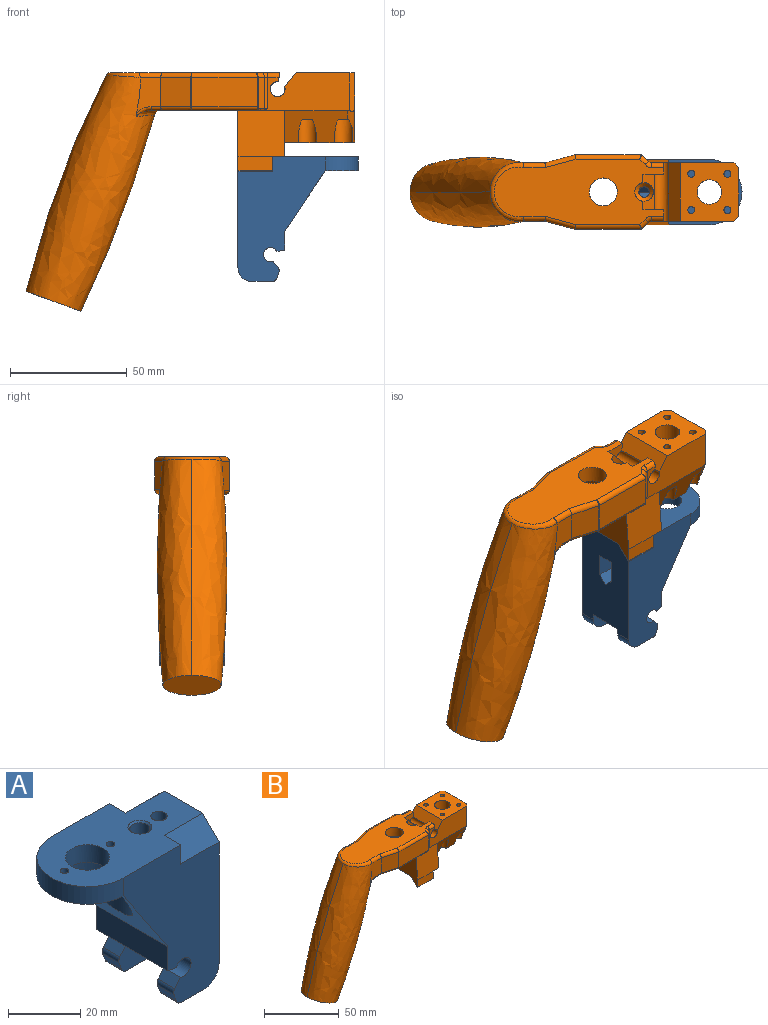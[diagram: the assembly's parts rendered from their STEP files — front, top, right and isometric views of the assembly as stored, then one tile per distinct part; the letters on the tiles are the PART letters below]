
ASSEMBLY  parts=2 mates=1
PART A: 52 faces, bbox 51.8x28x53.5 mm
  f0: cone r=1.4mm half-angle=59deg, axis (0,0,1), area 28.7mm2, adj f2
  f1: plane 13.5x0mm, normal (1,0,0), area 0mm2, adj f6,f7,f20,f22,f23
  f2: cylinder r=2.8mm len=7.5mm, axis (0,0,-1), area 131.9mm2, adj f0,f13
  f3: cylinder r=12.5mm len=25mm, axis (0,0,-1), area 464.3mm2, adj f4,f16
  f4: plane 28x26.99mm, normal (0,0,-1), area 426.9mm2, adj f3,f10,f11,f12,f15,f16
  f5: plane 6.11x6mm, normal (0,0,-1), area 28.3mm2, adj f17
  f6: plane 13.5x3.5mm, normal (0.87,-0.5,0), area 47.5mm2, adj f1,f20,f21,f22
  f7: plane 13.5x3.5mm, normal (0.87,0.5,0), area 47.5mm2, adj f1,f19,f20,f23
  f8: plane 6.5x6.5mm, normal (1,0,0), area 21.1mm2, adj f24,f25,f26
  f9: cylinder r=2.25mm len=12mm, axis (0,0,-1), area 169.6mm2, adj f20,f26
  f10: cylinder r=1.23mm len=6mm, axis (0,0,-1), area 46.4mm2, adj f4,f26
  f11: cylinder r=1.23mm len=6mm, axis (0,0,-1), area 46.4mm2, adj f4,f26
  f12: cylinder r=6.1mm len=12.2mm, axis (0,0,-1), area 230mm2, adj f4,f26
  f13: cone r=3.05mm half-angle=45deg, axis (0,0,1), area 13.6mm2, adj f2,f26
  f14: plane 6.5x6.5mm, normal (1,0,0), area 21.1mm2, adj f26,f27,f28
  f15: cylinder r=14mm len=28mm, axis (0,0,-1), area 263.9mm2, adj f4,f24,f26,f28
  f16: plane 28x26mm, normal (-0.83,0,-0.56), area 438mm2, adj f3,f4,f18,f24,f28
  f17: cylinder r=3mm len=6mm, axis (0,0,-1), area 94.2mm2, adj f5,f29
  f18: plane 28x8.14mm, normal (-1,0,0), area 227.9mm2, adj f16,f24,f28,f44
  f19: plane 11.52x10mm, normal (0,1,0), area 115.2mm2, adj f7,f20,f23,f45
  f20: plane 13.54x7mm, normal (0,0,-1), area 71.8mm2, adj f1,f6,f7,f9,f19,f21,f45
  f21: plane 11.52x10mm, normal (0,-1,0), area 115.2mm2, adj f6,f20,f22,f45
  f22: plane 13.54x3.5mm, normal (0,-0.71,0.71), area 62mm2, adj f1,f6,f21,f23,f45
  f23: plane 13.54x3.5mm, normal (0,0.71,0.71), area 62mm2, adj f1,f7,f19,f22,f45
  f24: plane 53.5x37.5mm, normal (0,1,0), area 1225.3mm2, adj f8,f15,f16,f18,f25,f26,f30,f31
  f25: plane 15x6.5mm, normal (0,0.71,0.71), area 137.9mm2, adj f8,f24,f26,f45
  f26: plane 51.76x28mm, normal (0,0,1), area 986.4mm2, adj f8,f9,f10,f11,f12,f13,f14,f15
  f27: plane 15x6.5mm, normal (0,-0.71,0.71), area 137.9mm2, adj f14,f26,f28,f45
  f28: plane 53.5x37.5mm, normal (0,-1,0), area 1225.3mm2, adj f14,f15,f16,f18,f26,f27,f37,f38
  f29: plane 8.15x8mm, normal (0,0,-1), area 22mm2, adj f17,f46
  f30: cylinder r=6mm len=6.5mm, axis (0,1,0), area 61.3mm2, adj f24,f31,f45,f47
  f31: plane 8.73x6.5mm, normal (0,0,-1), area 56.7mm2, adj f24,f30,f32,f47
  f32: cylinder r=2mm len=6.5mm, axis (0,1,0), area 15.8mm2, adj f24,f31,f33,f47
  f33: plane 6.5x2.66mm, normal (-0.94,0,-0.35), area 18.4mm2, adj f24,f32,f34,f47
  f34: cylinder r=2mm len=6.5mm, axis (0,-1,0), area 13.5mm2, adj f24,f33,f35,f47
  f35: plane 6.5x2.7mm, normal (-0.78,0,0.63), area 22.5mm2, adj f24,f34,f36,f47
  f36: cylinder r=3.05mm len=6.5mm, axis (0,-1,0), area 91.4mm2, adj f24,f35,f44,f47
  f37: cylinder r=6mm len=6.5mm, axis (0,1,0), area 61.3mm2, adj f28,f38,f45,f49
  f38: plane 8.73x6.5mm, normal (0,0,-1), area 56.7mm2, adj f28,f37,f39,f49
  f39: cylinder r=2mm len=6.5mm, axis (0,1,0), area 15.8mm2, adj f28,f38,f40,f49
  f40: plane 6.5x2.66mm, normal (-0.94,0,-0.35), area 18.4mm2, adj f28,f39,f41,f49
  f41: cylinder r=2mm len=6.5mm, axis (0,-1,0), area 13.5mm2, adj f28,f40,f42,f49
  f42: plane 6.5x2.7mm, normal (-0.78,0,0.63), area 22.5mm2, adj f28,f41,f43,f49
  f43: cylinder r=3.05mm len=6.5mm, axis (0,-1,0), area 91.4mm2, adj f28,f42,f44,f49
  f44: plane 28x3.28mm, normal (-0.16,0,-0.99), area 82.1mm2, adj f18,f24,f28,f36,f43,f47,f48,f49
  f45: plane 47.5x28mm, normal (1,0,0), area 1168mm2, adj f19,f20,f21,f22,f23,f24,f25,f26
  f46: cylinder r=4mm len=8mm, axis (0,0,1), area 175.9mm2, adj f29,f50
  f47: plane 17.74x15.25mm, normal (0,-1,0), area 145.3mm2, adj f30,f31,f32,f33,f34,f35,f36,f44
  f48: cylinder r=3.75mm len=15mm, axis (0,-1,0), area 153.6mm2, adj f44,f47,f49,f51
  f49: plane 17.74x15.25mm, normal (0,1,0), area 145.3mm2, adj f37,f38,f39,f40,f41,f42,f43,f44
  f50: plane 15x10.25mm, normal (0,0,-1), area 103.5mm2, adj f45,f46,f47,f49,f51
  f51: plane 15x2.96mm, normal (-1,0,0), area 44.4mm2, adj f47,f48,f49,f50
PART B: 105 faces, bbox 142.7x34x104.2 mm
  f0: plane 30.07x15.07mm, normal (0,0,-1), area 268.1mm2, adj f11,f12,f13,f28,f29,f45,f46,f97
  f1: cylinder r=1.5mm len=20mm, axis (0,0,1), area 188.5mm2, adj f43,f104
  f2: cylinder r=1.5mm len=20mm, axis (0,0,1), area 188.5mm2, adj f43,f101
  f3: cylinder r=1.5mm len=20mm, axis (0,0,1), area 188.5mm2, adj f43,f100
  f4: cylinder r=1.5mm len=20mm, axis (0,0,1), area 188.5mm2, adj f43,f98
  f5: plane 3.4x3.4mm, normal (0,0,-1), area 9.1mm2, adj f6
  f6: cone r=2.2mm half-angle=45deg, axis (0,0,1), area 19.5mm2, adj f5,f8
  f7: plane 6.5x6mm, normal (1,0,0), area 21mm2, adj f14,f15,f16,f17
  f8: cylinder r=2.7mm len=5.4mm, axis (0,0,-1), area 84.8mm2, adj f6,f17
  f9: plane 6.5x6mm, normal (1,0,0), area 21mm2, adj f17,f18,f19,f20
  f10: sphere r=1.5mm, area 0.6mm2, adj f24,f35,f36
  f11: cylinder r=5.25mm len=30mm, axis (0,0,-1), area 989.6mm2, adj f0,f43
  f12: plane 30x21mm, normal (1,0,0), area 524.6mm2, adj f0,f29,f30,f43,f44,f45
  f13: plane 28x19.74mm, normal (1,0,0), area 248.3mm2, adj f0,f17,f27,f28,f46,f47
  f14: plane 15x6mm, normal (0,1,0), area 90mm2, adj f7,f15,f47,f48
  f15: plane 15x0.5mm, normal (0,0,-1), area 7.5mm2, adj f7,f14,f16,f48
  f16: plane 15x6mm, normal (0,-0.71,-0.71), area 127.3mm2, adj f7,f15,f17,f48
  f17: plane 28x20mm, normal (0,0,-1), area 326.2mm2, adj f7,f8,f9,f13,f16,f18,f27,f31
  f18: plane 15x6mm, normal (0,0.71,-0.71), area 127.3mm2, adj f9,f17,f19,f48
  f19: plane 15x0.5mm, normal (0,0,-1), area 7.5mm2, adj f9,f18,f20,f48
  f20: plane 15x6mm, normal (0,-1,0), area 90mm2, adj f9,f19,f27,f48
  f21: bspline ~7.63x4.68mm, area 16.4mm2, adj f32,f33,f51,f52
  f22: plane 25.35x23.5mm, normal (-0.34,0,-0.94), area 490.9mm2, adj f52,f53
  f23: bspline ~7.09x4.19mm, area 11.6mm2, adj f33,f34,f53,f54
  f24: cylinder r=1.5mm len=12.5mm, axis (0,0,-1), area 4.9mm2, adj f10,f55,f56,f57
  f25: cylinder r=0.5mm len=12.5mm, axis (0,0,-1), area 4.9mm2, adj f26,f57,f58,f59
  f26: bspline ~1.53x1.5mm, area 1.3mm2, adj f25,f36,f37,f59
  f27: plane 20x19.74mm, normal (0,-1,0.08), area 395.9mm2, adj f13,f17,f20,f48,f61
  f28: plane 28.45x15.19mm, normal (0,-0.94,-0.34), area 264.8mm2, adj f0,f13,f29,f61,f97,f98,f99,f100
  f29: cylinder r=3mm len=18.04mm, axis (0,0.34,-0.94), area 48.4mm2, adj f0,f12,f28,f30,f61,f99,f100
  f30: plane 16.78x2mm, normal (0.71,-0.71,0), area 46mm2, adj f12,f29,f43,f61
  f31: cylinder r=2.25mm len=19.25mm, axis (0,0,-1), area 272.1mm2, adj f17,f62
  f32: cylinder r=2mm len=3.9mm, axis (-1,0,0), area 11.8mm2, adj f21,f49,f51,f64
  f33: bspline ~29.82x10.55mm, area 107.4mm2, adj f21,f23,f52,f53,f64
  f34: cylinder r=1.5mm len=4.25mm, axis (1,0,0), area 9.8mm2, adj f23,f35,f54,f64
  f35: cylinder r=1.5mm len=13.45mm, axis (-0.97,0.26,0), area 31.6mm2, adj f10,f34,f55,f64
  f36: cylinder r=1.5mm len=29.03mm, axis (-1,0,0), area 67.2mm2, adj f10,f26,f57,f64
  f37: cylinder r=0.5mm len=2.12mm, axis (-0.71,-0.71,0), area 2mm2, adj f26,f38,f59,f64
  f38: torus R=2.5mm, axis (0,0,-1), area 0.8mm2, adj f37,f60,f61,f64
  f39: plane 16x8.8mm, normal (0,1,0), area 140.8mm2, adj f40,f48,f50,f64
  f40: plane 25x8.8mm, normal (1,0,0), area 220mm2, adj f39,f41,f50,f64
  f41: plane 16x8.8mm, normal (0,-1,0), area 140.8mm2, adj f40,f48,f50,f64
  f42: plane 25x6.04mm, normal (-0.77,0,0.63), area 195.2mm2, adj f43,f61,f63,f65
  f43: plane 25x25mm, normal (0,0,1), area 506.1mm2, adj f1,f2,f3,f4,f11,f12,f30,f42
  f44: plane 16.78x2mm, normal (0.71,0.71,0), area 46mm2, adj f12,f43,f45,f65
  f45: cylinder r=3mm len=18.04mm, axis (0,0.34,0.94), area 48.4mm2, adj f0,f12,f44,f46,f65,f101,f102
  f46: plane 28.45x15.19mm, normal (0,0.94,-0.34), area 264.8mm2, adj f0,f13,f45,f65,f101,f102,f103,f104
  f47: plane 20x19.74mm, normal (0,1,0.08), area 395.9mm2, adj f13,f14,f17,f48,f65
  f48: plane 34.8x28mm, normal (-1,0,0), area 791.6mm2, adj f14,f15,f16,f17,f18,f19,f20,f27
  f49: cylinder r=2mm len=13.83mm, axis (-0.97,-0.26,0), area 42.5mm2, adj f32,f64,f67,f68
  f50: plane 25x16mm, normal (0,0,-1), area 286.9mm2, adj f39,f40,f41,f48,f69
  f51: plane 14.97x10.47mm, normal (0,1,0), area 114.9mm2, adj f21,f32,f52,f68,f70
  f52: bspline ~101.19x59.53mm, area 4291.9mm2, adj f21,f22,f33,f51,f53,f70,f71
  f53: bspline ~101.19x59.53mm, area 4291.7mm2, adj f22,f23,f33,f52,f54,f71,f72
  f54: plane 15.33x10.54mm, normal (0,-1,0), area 119.3mm2, adj f23,f34,f53,f55,f72
  f55: plane 12.87x12.5mm, normal (-0.26,-0.97,0), area 166.6mm2, adj f24,f35,f54,f73
  f56: sphere r=2mm, area 0.6mm2, adj f24,f73,f74
  f57: plane 28.03x12.5mm, normal (0,-1,0), area 350.4mm2, adj f24,f25,f36,f74
  f58: torus R=1.55mm, axis (0.92,0.38,0), area 0.6mm2, adj f25,f74,f75
  f59: plane 13.71x2.97mm, normal (0.71,-0.71,0), area 52.5mm2, adj f25,f26,f37,f60,f75
  f60: cylinder r=2mm len=13.5mm, axis (0,0,-1), area 21.2mm2, adj f38,f59,f61,f76
  f61: plane 48.21x16.48mm, normal (0,-1,0), area 507.9mm2, adj f27,f28,f29,f30,f38,f42,f43,f48
  f62: cone r=3.12mm half-angle=45deg, axis (0,0,1), area 48.6mm2, adj f31,f80
  f63: cylinder r=3.2mm len=25mm, axis (0,1,0), area 343.3mm2, adj f42,f61,f65,f78,f79,f81,f82,f83
  f64: plane 48.4x28.52mm, normal (0,0,-1), area 555mm2, adj f32,f33,f34,f35,f36,f37,f38,f39
  f65: plane 48.21x16.48mm, normal (0,1,0), area 507.9mm2, adj f42,f43,f44,f45,f46,f47,f48,f63
  f66: torus R=2.5mm, axis (0,0,-1), area 0.8mm2, adj f64,f65,f85,f86
  f67: cylinder r=2mm len=29.73mm, axis (-1,0,0), area 90.6mm2, adj f49,f64,f88,f89
  f68: plane 13.06x12mm, normal (-0.26,0.97,0), area 162.3mm2, adj f49,f51,f87,f89
  f69: cylinder r=6mm len=12mm, axis (0,0,-1), area 271.4mm2, adj f50,f90
  f70: cylinder r=2mm len=9.42mm, axis (1,0,0), area 28.7mm2, adj f51,f52,f71,f87,f90
  f71: bspline ~25.37x15.2mm, area 103.4mm2, adj f52,f53,f70,f72,f90
  f72: cylinder r=2mm len=9.42mm, axis (-1,0,0), area 28.7mm2, adj f53,f54,f71,f73,f90
  f73: cylinder r=2mm len=13.64mm, axis (-0.97,0.26,0), area 42.2mm2, adj f55,f56,f72,f90
  f74: cylinder r=2mm len=28.03mm, axis (-1,0,0), area 87mm2, adj f56,f57,f58,f90
  f75: cylinder r=2mm len=4.18mm, axis (-0.71,-0.71,0), area 11.3mm2, adj f58,f59,f76,f90
  f76: torus R=4mm, axis (0,0,1), area 6.7mm2, adj f60,f75,f77,f90
  f77: cylinder r=2mm len=5.17mm, axis (-1,0,0), area 15.7mm2, adj f61,f76,f78,f90
  f78: plane 5.04x3.96mm, normal (0.99,0,-0.16), area 18.1mm2, adj f61,f63,f77,f79,f90
  f79: plane 8.97x6.04mm, normal (0,1,0), area 30.9mm2, adj f63,f78,f81,f90
  f80: cylinder r=4mm len=15mm, axis (0,0,-1), area 339.7mm2, adj f62,f81,f90
  f81: plane 16.95x7.79mm, normal (0.77,0,0.63), area 72.7mm2, adj f63,f79,f80,f82,f90
  f82: plane 8.97x6.04mm, normal (0,-1,0), area 30.9mm2, adj f63,f81,f83,f90
  f83: plane 5.04x3.96mm, normal (0.99,0,-0.16), area 18.1mm2, adj f63,f65,f82,f84,f90
  f84: cylinder r=2mm len=5.17mm, axis (1,0,0), area 15.7mm2, adj f65,f83,f90,f91
  f85: cylinder r=0.5mm len=1.62mm, axis (-0.71,0.71,0), area 1.4mm2, adj f64,f66,f88,f92
  f86: cylinder r=2mm len=13.5mm, axis (0,0,1), area 21.2mm2, adj f65,f66,f91,f92
  f87: cylinder r=2mm len=13.83mm, axis (-0.97,-0.26,0), area 42.5mm2, adj f68,f70,f90,f93
  f88: bspline ~2.04x2mm, area 1.8mm2, adj f67,f85,f92,f94
  f89: plane 28.23x12mm, normal (0,1,0), area 338.8mm2, adj f67,f68,f93,f94
  f90: plane 72.77x28.01mm, normal (0,0,1), area 1463.4mm2, adj f69,f70,f71,f72,f73,f74,f75,f76
  f91: torus R=4mm, axis (0,0,1), area 6.7mm2, adj f84,f86,f90,f95
  f92: plane 13.81x3.08mm, normal (0.71,0.71,0), area 52.2mm2, adj f85,f86,f88,f94,f95
  f93: cylinder r=2mm len=28.23mm, axis (-1,0,0), area 87.3mm2, adj f87,f89,f90,f96
  f94: cylinder r=0.5mm len=12mm, axis (0,0,-1), area 4.7mm2, adj f88,f89,f92,f96
  f95: cylinder r=2mm len=4.18mm, axis (-0.71,0.71,0), area 11.3mm2, adj f90,f91,f92,f96
  f96: bspline ~2.03x2mm, area 0.5mm2, adj f93,f94,f95
  f97: cylinder r=4mm len=10mm, axis (0,0,-1), area 163.6mm2, adj f0,f28,f98
  f98: plane 8x7.39mm, normal (0,0,-1), area 41.4mm2, adj f4,f28,f97
  f99: cylinder r=4mm len=10mm, axis (0,0,-1), area 158.8mm2, adj f0,f28,f29,f100
  f100: plane 8.01x7.4mm, normal (0,0,-1), area 41.4mm2, adj f3,f28,f29,f99
  f101: plane 8.01x7.4mm, normal (0,0,-1), area 41.4mm2, adj f2,f45,f46,f102
  f102: cylinder r=4mm len=10mm, axis (0,0,-1), area 158.8mm2, adj f0,f45,f46,f101
  f103: cylinder r=4mm len=10mm, axis (0,0,-1), area 163.6mm2, adj f0,f46,f104
  f104: plane 8x7.39mm, normal (0,0,-1), area 41.4mm2, adj f1,f46,f103
PLACE A rot(axis=(0,0,1),180deg) t=(31.48,-6,-8)mm
PLACE B at identity
MATE fastened A.f0 <-> B.f8  axis (0,0,1) through (25,0,-8)mm
